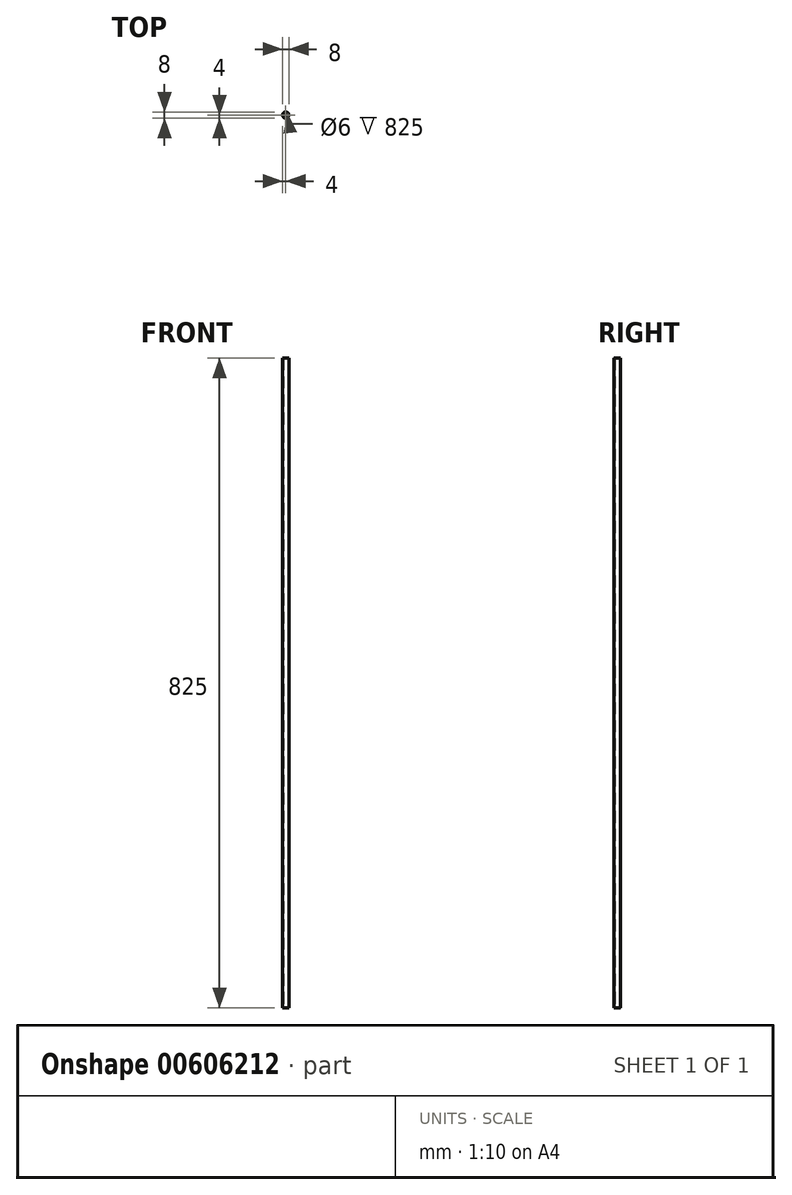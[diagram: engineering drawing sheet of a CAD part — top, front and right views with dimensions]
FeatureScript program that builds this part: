
annotation { "Feature Type Name" : "Feature", "Feature Type Description" : "" }
export const myFeature = defineFeature(function(context is Context, id is Id, definition is map)
    precondition{}
    {
        {
            var Q0;
            Q0=qCreatedBy(makeId("Top.planeOp"),FACE);
            var sketch = newSketch(context, id + "F0", { "sketchPlane" : qUnion([Q0])});
            skCircle(sketch, "E0", {"center": v(0, 0) * mm, "radius": 4 * mm});
            skCircle(sketch, "E1", {"center": v(0, 0) * mm, "radius": 3 * mm});
            skSolve(sketch);
        }
        {
            var Q0;
            Q0=makeQuery(id+"F0.imprint","IMPRINT",FACE,{"disambiguationData":[TD([[makeQuery(id+"F0.imprint","IMPRINT",EDGE,{"derivedFrom":sQuery(id+"F0.wireOp",EDGE,"E0")}),1.0]])]});
            extrude(context, id + "F1", {"entities" : qUnion([Q0]), "depth" : 825 * mm, "offsetDistance" : 25 * mm});
        }
    });
